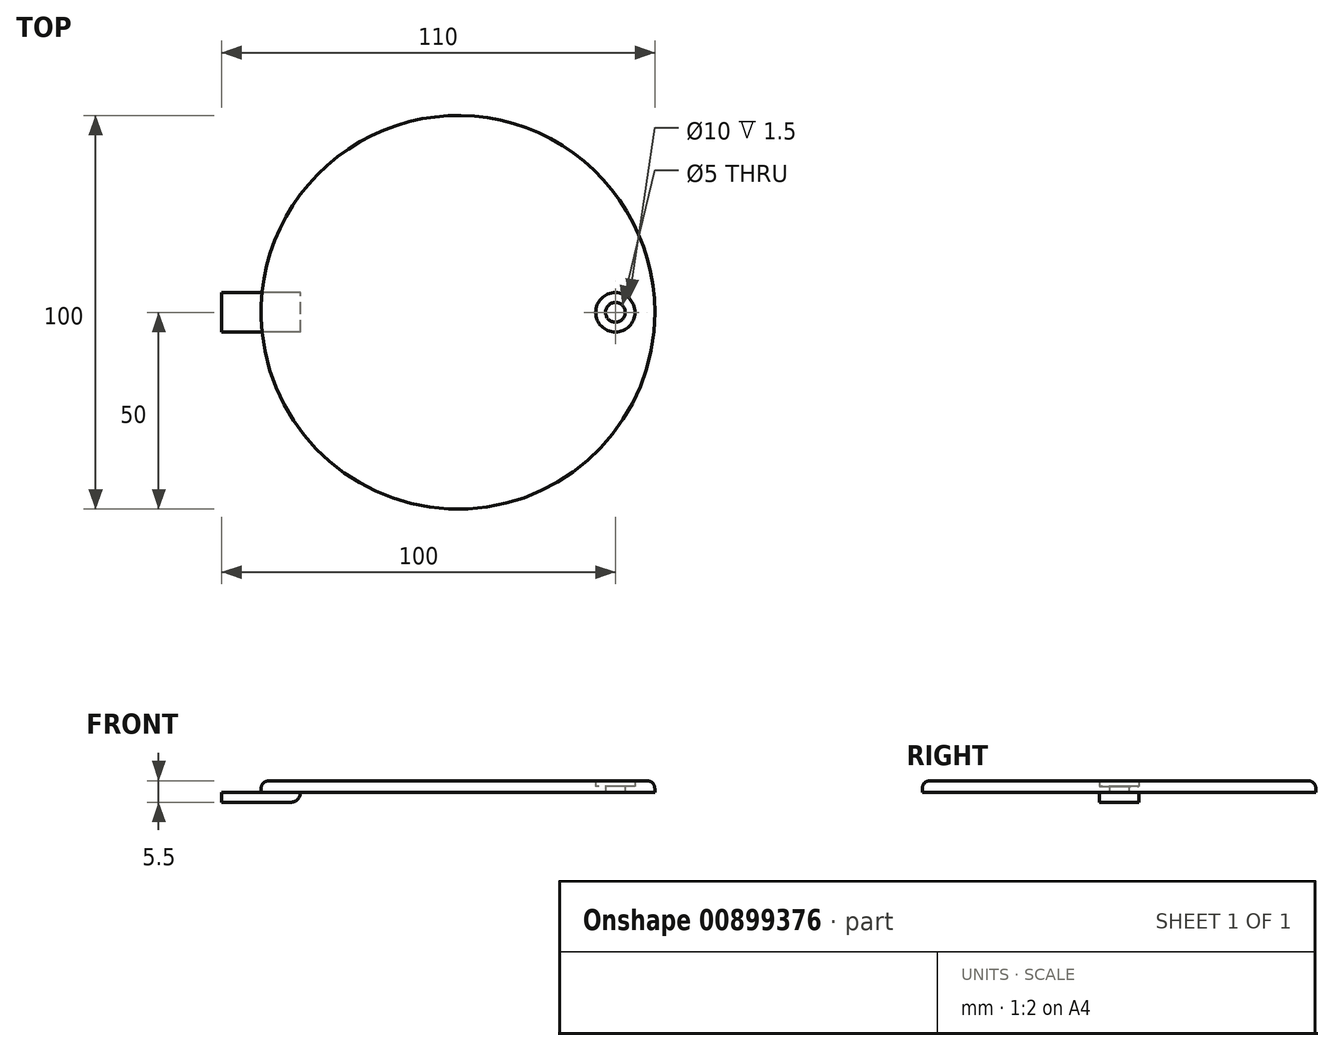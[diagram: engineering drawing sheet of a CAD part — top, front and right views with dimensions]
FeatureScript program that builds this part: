
annotation { "Feature Type Name" : "Feature", "Feature Type Description" : "" }
export const myFeature = defineFeature(function(context is Context, id is Id, definition is map)
    precondition{}
    {
        {
            var Q0;
            Q0=qCreatedBy(makeId("Top.planeOp"),FACE);
            var sketch = newSketch(context, id + "F0", { "sketchPlane" : qUnion([Q0])});
            skCircle(sketch, "E0", {"center": v(0, 0) * mm, "radius": 50 * mm});
            skLineSegment(sketch, "E1", {"start": v(-50, 0) * mm, "end": v(50, 0) * mm, "construction": true});
            skLineSegment(sketch, "E2.bottom", {"start": v(-40, -5) * mm, "end": v(-60, -5) * mm});
            skLineSegment(sketch, "E2.top", {"start": v(-40, 5) * mm, "end": v(-60, 5) * mm});
            skLineSegment(sketch, "E2.left", {"start": v(-40, -5) * mm, "end": v(-40, 5) * mm});
            skLineSegment(sketch, "E2.right", {"start": v(-60, -5) * mm, "end": v(-60, 5) * mm});
            skPoint(sketch, "E2.middle", {"position": v(-50, 0) * mm});
            skLineSegment(sketch, "E3", {"start": v(50, 0) * mm, "end": v(40, 0) * mm, "construction": true});
            skCircle(sketch, "E4", {"center": v(40, 0) * mm, "radius": 5 * mm});
            skCircle(sketch, "E5", {"center": v(40, 0) * mm, "radius": 2.5 * mm});
            skSolve(sketch);
        }
        {
            var Q0;
            {var subQ0=sQuery(id+"F0.wireOp",EDGE,"E2.left");Q0=makeQuery(id+"F0.imprint","IMPRINT",FACE,{"disambiguationData":[TD([[makeQuery(id+"F0.imprint","IMPRINT",EDGE,{"derivedFrom":subQ0}),-1.0]])]});}
            var Q1;
            {var subQ5=sQuery(id+"F0.wireOp",EDGE,"E2.left");Q1=makeQuery(id+"F0.imprint","IMPRINT",FACE,{"disambiguationData":[TD([[makeQuery(id+"F0.imprint","IMPRINT",EDGE,{"derivedFrom":subQ5}),1.0]])]});}
            extrude(context, id + "F1", {"entities" : qUnion([Q0, Q1]), "depth" : 3 * mm, "offsetDistance" : 25 * mm});
        }
        {
            var Q0;
            Q0=makeQuery(id+"F0.imprint","IMPRINT",FACE,{"disambiguationData":[TD([[makeQuery(id+"F0.imprint","IMPRINT",EDGE,{"derivedFrom":sQuery(id+"F0.wireOp",EDGE,"E4")}),1.0]])]});
            extrude(context, id + "F2", {"entities" : qUnion([Q0]), "operationType" : NewBodyOperationType.ADD, "depth" : 1.5 * mm, "offsetDistance" : 25 * mm});
        }
        {
            var Q0;
            {var subQ5=sQuery(id+"F0.wireOp",EDGE,"E2.right");Q0=makeQuery(id+"F0.imprint","IMPRINT",FACE,{"disambiguationData":[TD([[makeQuery(id+"F0.imprint","IMPRINT",EDGE,{"derivedFrom":subQ5}),-1.0]])]});}
            var Q1;
            {var subQ5=sQuery(id+"F0.wireOp",EDGE,"E2.left");Q1=makeQuery(id+"F0.imprint","IMPRINT",FACE,{"disambiguationData":[TD([[makeQuery(id+"F0.imprint","IMPRINT",EDGE,{"derivedFrom":subQ5}),1.0]])]});}
            extrude(context, id + "F3", {"entities" : qUnion([Q0, Q1]), "operationType" : NewBodyOperationType.ADD, "oppositeDirection" : true, "depth" : 2.5 * mm, "offsetDistance" : 25 * mm});
        }
        {
            var Q0;
            Q0=makeQuery(id+"F3.opExtrude","CAP_EDGE",EDGE,{"disambiguationData":[OSD([sQuery(id+"F0.wireOp",EDGE,"E2.left")])],"isStart":false});
            fillet(context, id + "F4", {"entities" : qUnion([Q0]), "radius" : 2.5 * mm, "tangentPropagation" : true, "allowEdgeOverflow" : false});
        }
        {
            var Q0;
            Q0=makeQuery(id+"F1.opExtrude","CAP_EDGE",EDGE,{"disambiguationData":[OSD([sQuery(id+"F0.wireOp",EDGE,"E0")])],"isStart":false});
            fillet(context, id + "F5", {"entities" : qUnion([Q0]), "radius" : 2 * mm, "tangentPropagation" : true, "allowEdgeOverflow" : false});
        }
    });
